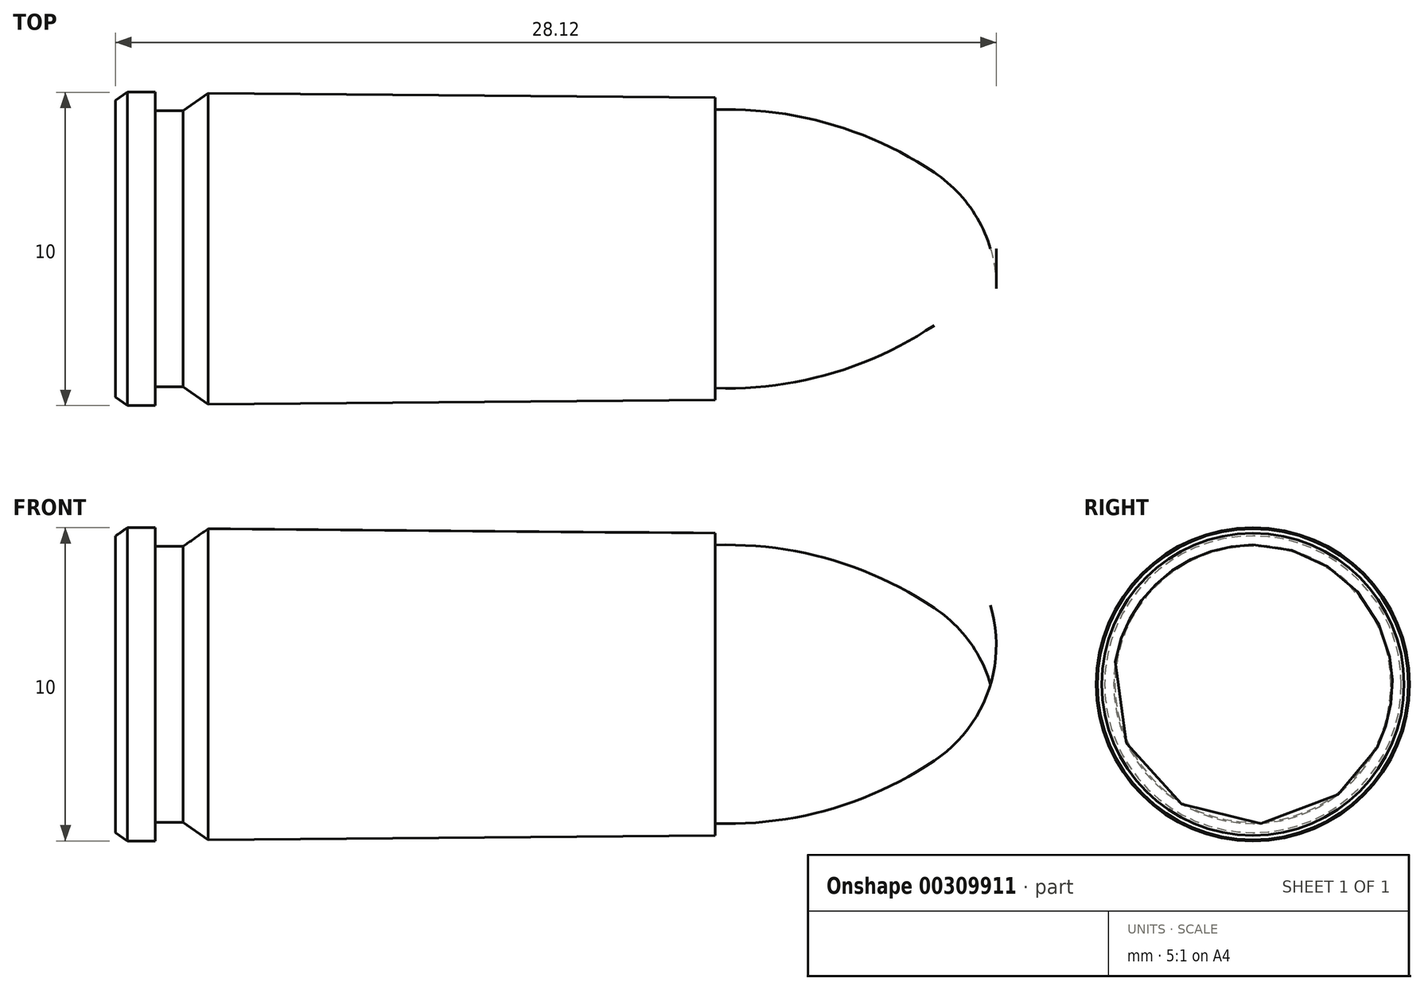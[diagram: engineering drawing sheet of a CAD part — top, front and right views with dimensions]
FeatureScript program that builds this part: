
annotation { "Feature Type Name" : "Feature", "Feature Type Description" : "" }
export const myFeature = defineFeature(function(context is Context, id is Id, definition is map)
    precondition{}
    {
        {
            var Q0;
            Q0=qCreatedBy(makeId("Front.planeOp"),FACE);
            var sketch = newSketch(context, id + "F0", { "sketchPlane" : qUnion([Q0])});
            skLineSegment(sketch, "E0", {"start": v(-59.91, 0) * mm, "end": v(98.1, 0) * mm});
            skLineSegment(sketch, "E1", {"start": v(0, 0) * mm, "end": v(0, 4.74) * mm});
            skLineSegment(sketch, "E2", {"start": v(0, 4.74) * mm, "end": v(0.38, 5) * mm});
            skLineSegment(sketch, "E3", {"start": v(0.38, 5) * mm, "end": v(1.27, 5) * mm});
            skLineSegment(sketch, "E4", {"start": v(1.27, 5) * mm, "end": v(1.27, 4.4) * mm});
            skLineSegment(sketch, "E5", {"start": v(1.27, 4.4) * mm, "end": v(2.16, 4.4) * mm});
            skLineSegment(sketch, "E6", {"start": v(2.16, 4.4) * mm, "end": v(2.96, 4.97) * mm});
            skLineSegment(sketch, "E7", {"start": v(2.96, 4.97) * mm, "end": v(19.15, 4.83) * mm});
            skLineSegment(sketch, "E8", {"start": v(19.15, 4.83) * mm, "end": v(19.15, 4.45) * mm});
            skLineSegment(sketch, "E9", {"start": v(27.94, 6.75) * mm, "end": v(27.94, -5.66) * mm});
            skArc(sketch, "E10", {"start": v(27.94, 0) * mm, "mid": v(27.25, 1.38) * mm, "end": v(26.14, 2.44) * mm});
            skArc(sketch, "E11", {"start": v(26.14, 2.44) * mm, "mid": v(22.8, 4) * mm, "end": v(19.15, 4.44) * mm});
            skSolve(sketch);
        }
        {
            var Q0;
            {var subQ1=sQuery(id+"F0.wireOp",EDGE,"E1");Q0=makeQuery(id+"F0.imprint","IMPRINT",FACE,{"disambiguationData":[TD([[makeQuery(id+"F0.imprint","IMPRINT",EDGE,{"derivedFrom":subQ1}),-1.0]])]});}
            var Q1;
            Q1=sQuery(id+"F0.wireOp",EDGE,"E0");
            revolve(context, id + "F1", {"entities" : qUnion([Q0]), "axis" : qUnion([Q1]), "revolveType" : RevolveType.FULL});
        }
    });
